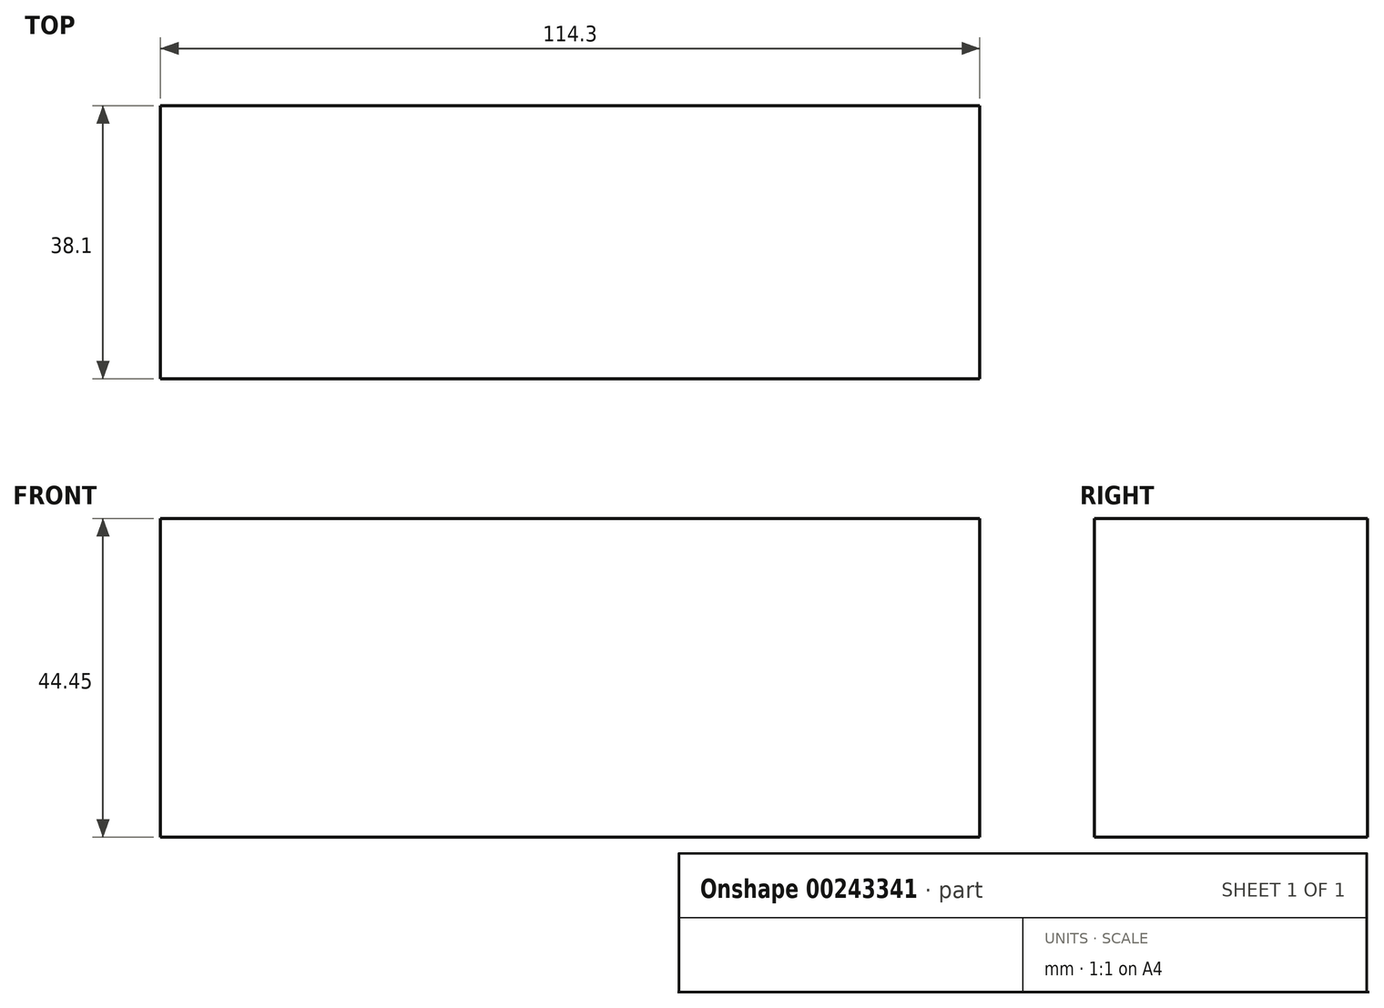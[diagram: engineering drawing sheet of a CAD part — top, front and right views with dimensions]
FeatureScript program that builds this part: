
annotation { "Feature Type Name" : "Feature", "Feature Type Description" : "" }
export const myFeature = defineFeature(function(context is Context, id is Id, definition is map)
    precondition{}
    {
        {
            var Q0;
            Q0=qCreatedBy(makeId("Top.planeOp"),FACE);
            var sketch = newSketch(context, id + "F0", { "sketchPlane" : qUnion([Q0])});
            skLineSegment(sketch, "E0.bottom", {"start": v(-57.15, 19.05) * mm, "end": v(57.15, 19.05) * mm});
            skLineSegment(sketch, "E0.top", {"start": v(-57.15, -19.05) * mm, "end": v(57.15, -19.05) * mm});
            skLineSegment(sketch, "E0.left", {"start": v(-57.15, 19.05) * mm, "end": v(-57.15, -19.05) * mm});
            skLineSegment(sketch, "E0.right", {"start": v(57.15, 19.05) * mm, "end": v(57.15, -19.05) * mm});
            skPoint(sketch, "E0.middle", {"position": v(0, 0) * mm});
            skSolve(sketch);
        }
        {
            var Q0;
            Q0 = qSketchRegion(id + "F0", true);
            extrude(context, id + "F1", {"entities" : qUnion([Q0]), "depth" : 44.45 * mm});
        }
    });
